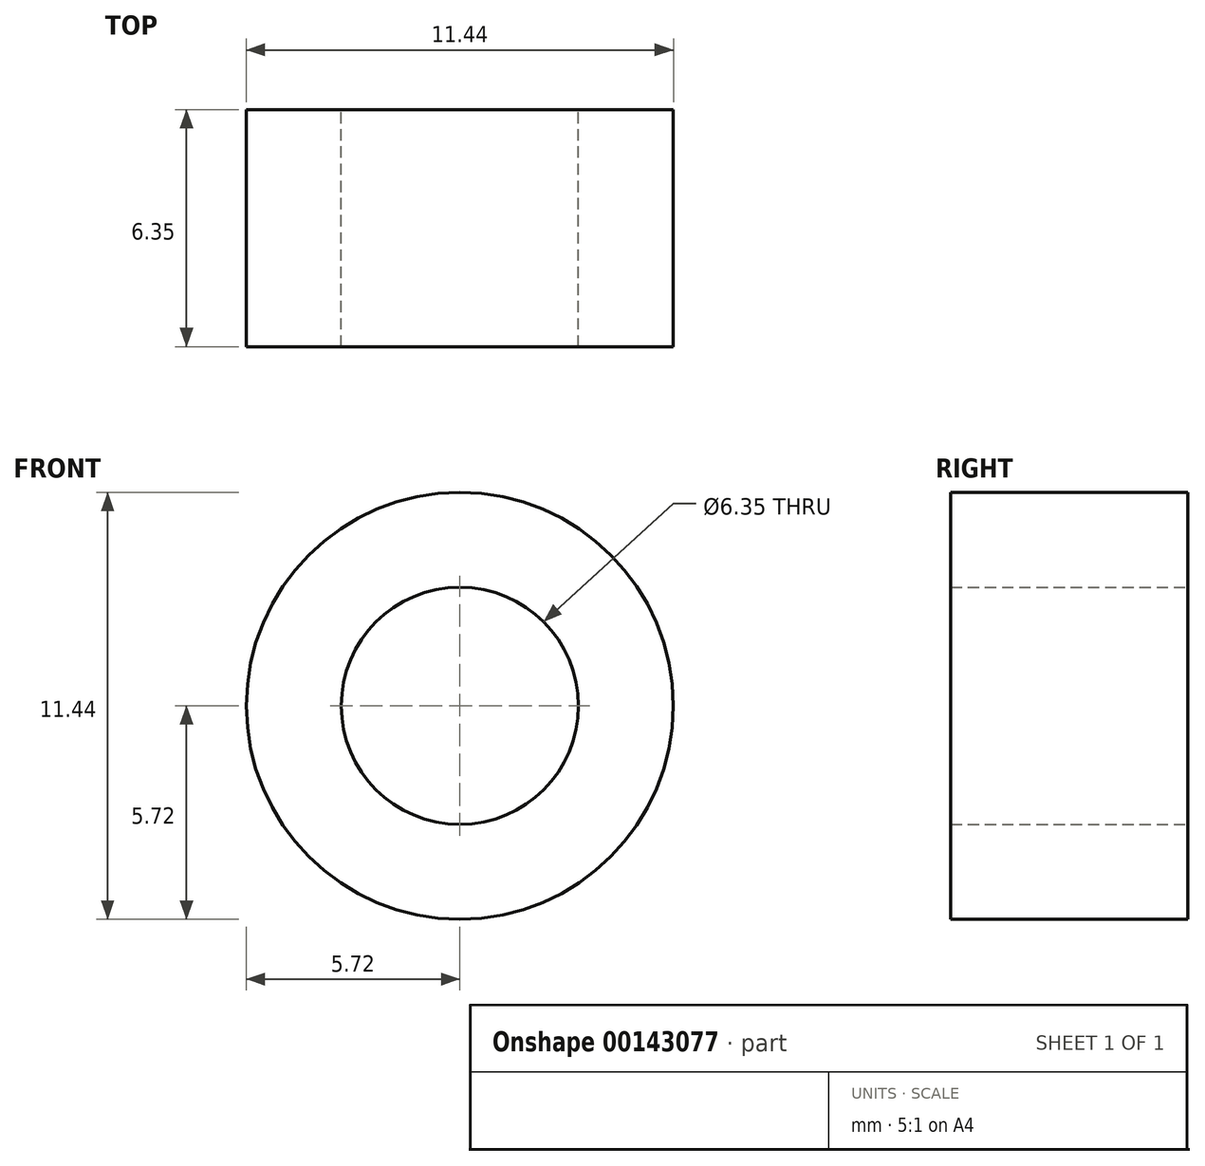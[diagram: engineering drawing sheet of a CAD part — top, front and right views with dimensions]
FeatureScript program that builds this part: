
annotation { "Feature Type Name" : "Feature", "Feature Type Description" : "" }
export const myFeature = defineFeature(function(context is Context, id is Id, definition is map)
    precondition{}
    {
        {
            var Q0;
            Q0=qCreatedBy(makeId("Front.planeOp"),FACE);
            var sketch = newSketch(context, id + "F0", { "sketchPlane" : qUnion([Q0])});
            skCircle(sketch, "E0", {"center": v(0, 0) * mm, "radius": 5.72 * mm});
            skCircle(sketch, "E1", {"center": v(0, 0) * mm, "radius": 3.18 * mm});
            skSolve(sketch);
        }
        {
            var Q0;
            Q0=makeQuery(id+"F0.imprint","IMPRINT",FACE,{"disambiguationData":[TD([[makeQuery(id+"F0.imprint","IMPRINT",EDGE,{"derivedFrom":sQuery(id+"F0.wireOp",EDGE,"E0")}),1.0]])]});
            extrude(context, id + "F1", {"entities" : qUnion([Q0]), "depth" : 6.35 * mm});
        }
    });
